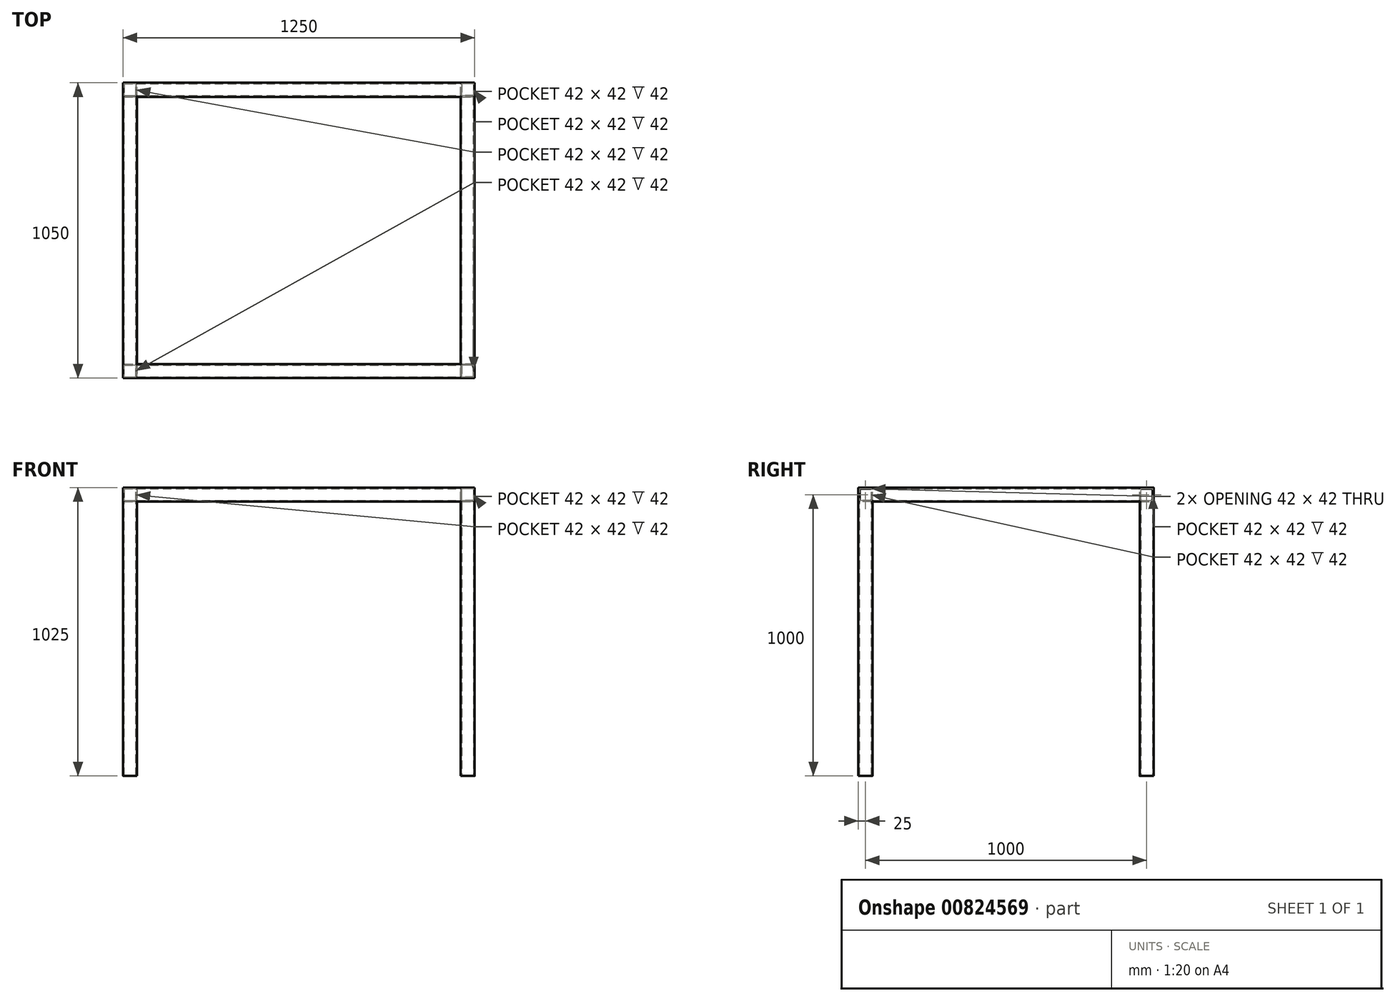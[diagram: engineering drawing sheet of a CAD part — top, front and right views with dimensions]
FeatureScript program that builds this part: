
annotation { "Feature Type Name" : "Feature", "Feature Type Description" : "" }
export const myFeature = defineFeature(function(context is Context, id is Id, definition is map)
    precondition{}
    {
        {
            var Q0;
            Q0=qCreatedBy(makeId("Right.planeOp"),FACE);
            var sketch = newSketch(context, id + "F0", { "sketchPlane" : qUnion([Q0])});
            skLineSegment(sketch, "E0", {"start": v(0, 0) * mm, "end": v(0, 1000) * mm});
            skLineSegment(sketch, "E1", {"start": v(0, 1000) * mm, "end": v(1000, 1000) * mm});
            skLineSegment(sketch, "E2", {"start": v(1000, 1000) * mm, "end": v(1000, 0) * mm});
            skSolve(sketch);
        }
        {
            var Q0;
            Q0=qCreatedBy(makeId("Top.planeOp"),FACE);
            var sketch = newSketch(context, id + "F1", { "sketchPlane" : qUnion([Q0])});
            skLineSegment(sketch, "E3.bottom", {"start": v(20, -25) * mm, "end": v(-20, -25) * mm});
            skLineSegment(sketch, "E3.top", {"start": v(20, 25) * mm, "end": v(-20, 25) * mm});
            skLineSegment(sketch, "E3.left", {"start": v(25, -20) * mm, "end": v(25, 20) * mm});
            skLineSegment(sketch, "E3.right", {"start": v(-25, -20) * mm, "end": v(-25, 20) * mm});
            skPoint(sketch, "E3.middle", {"position": v(0, 0) * mm});
            skPoint(sketch, "E4.visualSharp", {"position": v(25, 25) * mm});
            skArc(sketch, "E4.filletArc", {"start": v(25, 20) * mm, "mid": v(23.54, 23.54) * mm, "end": v(20, 25) * mm});
            skPoint(sketch, "E5.visualSharp", {"position": v(-25, 25) * mm});
            skArc(sketch, "E5.filletArc", {"start": v(-20, 25) * mm, "mid": v(-23.54, 23.54) * mm, "end": v(-25, 20) * mm});
            skPoint(sketch, "E6.visualSharp", {"position": v(-25, -25) * mm});
            skArc(sketch, "E6.filletArc", {"start": v(-25, -20) * mm, "mid": v(-23.54, -23.54) * mm, "end": v(-20, -25) * mm});
            skPoint(sketch, "E7.visualSharp", {"position": v(25, -25) * mm});
            skArc(sketch, "E7.filletArc", {"start": v(20, -25) * mm, "mid": v(23.54, -23.54) * mm, "end": v(25, -20) * mm});
            skLineSegment(sketch, "E8.0", {"start": v(21, 21) * mm, "end": v(-21, 21) * mm});
            skLineSegment(sketch, "E8.1", {"start": v(21, -21) * mm, "end": v(21, 21) * mm});
            skLineSegment(sketch, "E8.2", {"start": v(21, -21) * mm, "end": v(-21, -21) * mm});
            skLineSegment(sketch, "E8.3", {"start": v(-21, -21) * mm, "end": v(-21, 21) * mm});
            skSolve(sketch);
        }
        {
            var Q0;
            Q0=makeQuery(id+"F1.imprint","IMPRINT",FACE,{"disambiguationData":[TD([[makeQuery(id+"F1.imprint","IMPRINT",EDGE,{"derivedFrom":sQuery(id+"F1.wireOp",EDGE,"E3.bottom")}),-1.0]])]});
            var Q1;
            Q1=sQuery(id+"F0.wireOp",EDGE,"E0");
            var Q2;
            Q2=sQuery(id+"F0.wireOp",EDGE,"E1");
            var Q3;
            Q3=sQuery(id+"F0.wireOp",EDGE,"E2");
            sweep(context, id + "F2", {"profiles" : qUnion([Q0]), "path" : qUnion([Q1, Q2, Q3])});
        }
        {
            var Q0;
            Q0=makeQuery(id+"F2.opSweep","SWEPT_FACE",FACE,{"disambiguationData":[OSD([sQuery(id+"F0.wireOp",EDGE,"E0"),sQuery(id+"F1.wireOp",EDGE,"E3.right")])]});
            var sketch = newSketch(context, id + "F3", { "sketchPlane" : qUnion([Q0])});
            skLineSegment(sketch, "E9.bottom", {"start": v(-980, 975) * mm, "end": v(-1020, 975) * mm});
            skLineSegment(sketch, "E9.top", {"start": v(-980, 1025) * mm, "end": v(-1020, 1025) * mm});
            skLineSegment(sketch, "E9.left", {"start": v(-975, 980) * mm, "end": v(-975, 1020) * mm});
            skLineSegment(sketch, "E9.right", {"start": v(-1025, 980) * mm, "end": v(-1025, 1020) * mm});
            skPoint(sketch, "E9.middle", {"position": v(-1000, 1000) * mm});
            skPoint(sketch, "E10.visualSharp", {"position": v(-975, 1025) * mm});
            skArc(sketch, "E10.filletArc", {"start": v(-975, 1020) * mm, "mid": v(-976.46, 1023.54) * mm, "end": v(-980, 1025) * mm});
            skPoint(sketch, "E11.visualSharp", {"position": v(-1025, 1025) * mm});
            skArc(sketch, "E11.filletArc", {"start": v(-1020, 1025) * mm, "mid": v(-1023.54, 1023.54) * mm, "end": v(-1025, 1020) * mm});
            skPoint(sketch, "E12.visualSharp", {"position": v(-1025, 975) * mm});
            skArc(sketch, "E12.filletArc", {"start": v(-1025, 980) * mm, "mid": v(-1023.54, 976.46) * mm, "end": v(-1020, 975) * mm});
            skPoint(sketch, "E13.visualSharp", {"position": v(-975, 975) * mm});
            skArc(sketch, "E13.filletArc", {"start": v(-980, 975) * mm, "mid": v(-976.46, 976.46) * mm, "end": v(-975, 980) * mm});
            skLineSegment(sketch, "E14.0", {"start": v(-979, 1021) * mm, "end": v(-1021, 1021) * mm});
            skLineSegment(sketch, "E14.1", {"start": v(-979, 979) * mm, "end": v(-979, 1021) * mm});
            skLineSegment(sketch, "E14.2", {"start": v(-979, 979) * mm, "end": v(-1021, 979) * mm});
            skLineSegment(sketch, "E14.3", {"start": v(-1021, 979) * mm, "end": v(-1021, 1021) * mm});
            skLineSegment(sketch, "E15", {"start": v(-500, 980) * mm, "end": v(-500, 1065.5) * mm, "construction": true});
            skArc(sketch, "E16.MirrorCS", {"start": v(-20, 975) * mm, "mid": v(-23.54, 976.46) * mm, "end": v(-25, 980) * mm});
            skArc(sketch, "E17.MirrorCS", {"start": v(-25, 1020) * mm, "mid": v(-23.54, 1023.54) * mm, "end": v(-20, 1025) * mm});
            skArc(sketch, "E18.MirrorCS", {"start": v(20, 1025) * mm, "mid": v(23.54, 1023.54) * mm, "end": v(25, 1020) * mm});
            skArc(sketch, "E19.MirrorCS", {"start": v(25, 980) * mm, "mid": v(23.54, 976.46) * mm, "end": v(20, 975) * mm});
            skLineSegment(sketch, "E20.MirrorCS", {"start": v(-20, 1025) * mm, "end": v(20, 1025) * mm});
            skLineSegment(sketch, "E21.MirrorCS", {"start": v(-21, 1021) * mm, "end": v(21, 1021) * mm});
            skPoint(sketch, "E22.MirrorP", {"position": v(25, 1025) * mm});
            skLineSegment(sketch, "E23.MirrorCS", {"start": v(-20, 975) * mm, "end": v(20, 975) * mm});
            skLineSegment(sketch, "E24.MirrorCS", {"start": v(-25, 980) * mm, "end": v(-25, 1020) * mm});
            skLineSegment(sketch, "E25.MirrorCS", {"start": v(25, 980) * mm, "end": v(25, 1020) * mm});
            skLineSegment(sketch, "E26.MirrorCS", {"start": v(-21, 979) * mm, "end": v(-21, 1021) * mm});
            skPoint(sketch, "E27.MirrorP", {"position": v(25, 975) * mm});
            skPoint(sketch, "E28.MirrorP", {"position": v(-25, 1025) * mm});
            skLineSegment(sketch, "E29.MirrorCS", {"start": v(-21, 979) * mm, "end": v(21, 979) * mm});
            skPoint(sketch, "E30.MirrorP", {"position": v(0, 1000) * mm});
            skLineSegment(sketch, "E31.MirrorCS", {"start": v(21, 979) * mm, "end": v(21, 1021) * mm});
            skPoint(sketch, "E32.MirrorP", {"position": v(-25, 975) * mm});
            skSolve(sketch);
        }
        {
            var Q0;
            Q0 = qSketchRegion(id + "F3", true);
            extrude(context, id + "F4", {"entities" : qUnion([Q0]), "operationType" : NewBodyOperationType.ADD, "depth" : (1000 + 200) * mm, "offsetDistance" : 25 * mm});
        }
        {
            var Q0;
            Q0=qCreatedBy(makeId("Right.planeOp"),FACE);
            cPlane(context, id + "F5", {"entities" : qUnion([Q0]), "cplaneType" : CPlaneType.OFFSET, "offset" : (1200 / 2) * mm, "oppositeDirection" : true, "width" : 150 * mm, "height" : 150 * mm});
        }
        {
            var Q0;
            Q0=makeQuery(id+"F2.opSweep","SWEPT_BODY",BODY,{"disambiguationData":[OSD([sQuery(id+"F0.wireOp",EDGE,"E2"),sQuery(id+"F1.wireOp",EDGE,"E3.bottom"),sQuery(id+"F1.wireOp",EDGE,"E3.top"),sQuery(id+"F1.wireOp",EDGE,"E3.left"),sQuery(id+"F1.wireOp",EDGE,"E3.right"),sQuery(id+"F1.wireOp",EDGE,"E4.filletArc"),sQuery(id+"F1.wireOp",EDGE,"E5.filletArc"),sQuery(id+"F1.wireOp",EDGE,"E6.filletArc"),sQuery(id+"F1.wireOp",EDGE,"E7.filletArc"),sQuery(id+"F1.wireOp",EDGE,"E8.0"),sQuery(id+"F1.wireOp",EDGE,"E8.1"),sQuery(id+"F1.wireOp",EDGE,"E8.2"),sQuery(id+"F1.wireOp",EDGE,"E8.3")])]});
            var Q1;
            Q1=qCreatedBy(id+"F5.planeOp",FACE);
            mirror(context, id + "F6", {"operationType" : NewBodyOperationType.ADD, "entities" : qUnion([Q0]), "mirrorPlane" : qUnion([Q1])});
        }
    });
